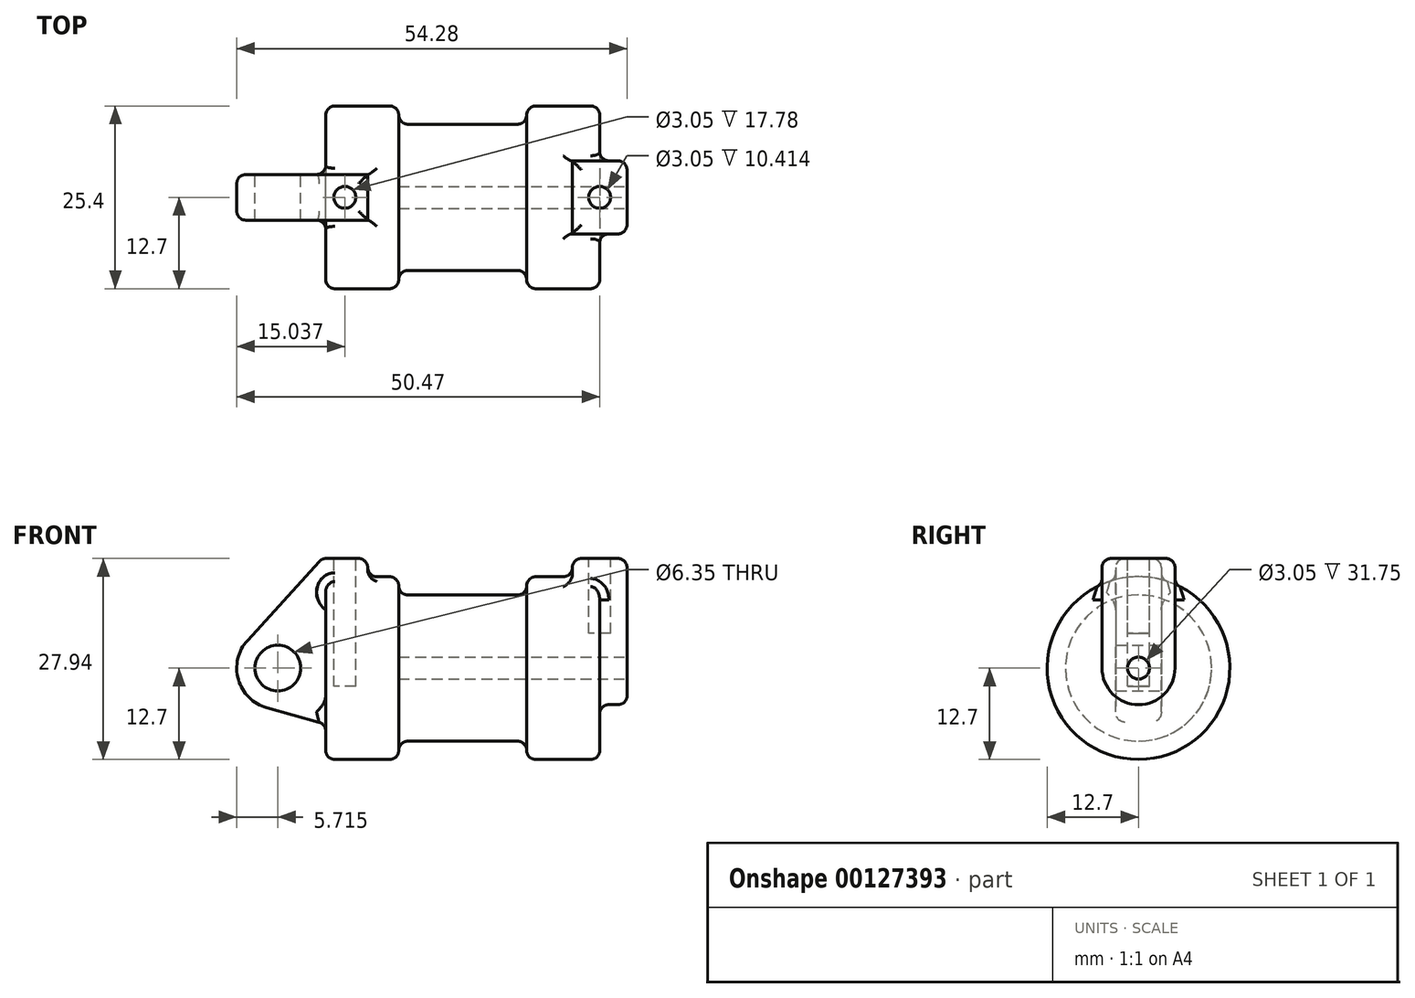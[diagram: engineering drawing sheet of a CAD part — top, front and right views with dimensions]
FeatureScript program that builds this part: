
annotation { "Feature Type Name" : "Feature", "Feature Type Description" : "" }
export const myFeature = defineFeature(function(context is Context, id is Id, definition is map)
    precondition{}
    {
        {
            var Q0;
            Q0=qCreatedBy(makeId("Front.planeOp"),FACE);
            var sketch = newSketch(context, id + "F0", { "sketchPlane" : qUnion([Q0])});
            skLineSegment(sketch, "E0", {"start": v(0, 0) * mm, "end": v(0, 12.7) * mm});
            skLineSegment(sketch, "E1", {"start": v(0, 12.7) * mm, "end": v(10.16, 12.7) * mm});
            skLineSegment(sketch, "E2", {"start": v(10.16, 12.7) * mm, "end": v(10.16, 10.16) * mm});
            skLineSegment(sketch, "E3", {"start": v(10.16, 10.16) * mm, "end": v(27.94, 10.16) * mm});
            skLineSegment(sketch, "E4", {"start": v(27.94, 10.16) * mm, "end": v(27.94, 12.7) * mm});
            skLineSegment(sketch, "E5", {"start": v(27.94, 12.7) * mm, "end": v(38.1, 12.7) * mm});
            skLineSegment(sketch, "E6", {"start": v(38.1, 12.7) * mm, "end": v(38.1, 0) * mm});
            skLineSegment(sketch, "E7", {"start": v(38.1, 0) * mm, "end": v(0, 0) * mm});
            skLineSegment(sketch, "E8", {"start": v(5.84, 15.24) * mm, "end": v(-0.5, 15.24) * mm});
            skLineSegment(sketch, "E9", {"start": v(-0.5, 15.24) * mm, "end": v(-10.88, 3.85) * mm});
            skLineSegment(sketch, "E10", {"start": v(0, 0) * mm, "end": v(-6.65, 0) * mm});
            skCircle(sketch, "E11", {"center": v(-6.65, 0) * mm, "radius": 5.72 * mm});
            skCircle(sketch, "E12", {"center": v(-6.65, 0) * mm, "radius": 3.18 * mm});
            skLineSegment(sketch, "E13", {"start": v(5.84, 15.24) * mm, "end": v(5.84, -9.4) * mm});
            skLineSegment(sketch, "E14", {"start": v(5.84, -9.4) * mm, "end": v(-8.18, -5.5) * mm});
            skSolve(sketch);
        }
        {
            var Q0;
            {var subQ0=sQuery(id+"F0.wireOp",EDGE,"E0");Q0=makeQuery(id+"F0.imprint","IMPRINT",FACE,{"disambiguationData":[TD([[makeQuery(id+"F0.imprint","IMPRINT",EDGE,{"derivedFrom":subQ0}),-1.0]])]});}
            var Q1;
            {var subQ0=sQuery(id+"F0.wireOp",EDGE,"E2");Q1=makeQuery(id+"F0.imprint","IMPRINT",FACE,{"disambiguationData":[TD([[makeQuery(id+"F0.imprint","IMPRINT",EDGE,{"derivedFrom":subQ0}),-1.0]])]});}
            var Q2;
            Q2=sQuery(id+"F0.wireOp",EDGE,"E7");
            revolve(context, id + "F1", {"entities" : qUnion([Q0, Q1]), "axis" : qUnion([Q2]), "revolveType" : RevolveType.FULL});
        }
        {
            var Q0;
            {var subQ3=sQuery(id+"F0.wireOp",EDGE,"E0");Q0=makeQuery(id+"F0.imprint","IMPRINT",FACE,{"disambiguationData":[TD([[makeQuery(id+"F0.imprint","IMPRINT",EDGE,{"derivedFrom":subQ3}),1.0]])]});}
            var Q1;
            {var subQ4=sQuery(id+"F0.wireOp",EDGE,"E12");Q1=makeQuery(id+"F0.imprint","IMPRINT",FACE,{"disambiguationData":[TD([[makeQuery(id+"F0.imprint","IMPRINT",EDGE,{"derivedFrom":subQ4}),-1.0]])]});}
            var Q2;
            {var subQ0=sQuery(id+"F0.wireOp",EDGE,"E14");Q2=makeQuery(id+"F0.imprint","IMPRINT",FACE,{"disambiguationData":[TD([[makeQuery(id+"F0.imprint","IMPRINT",EDGE,{"derivedFrom":subQ0}),-1.0]])]});}
            var Q3;
            {var subQ0=sQuery(id+"F0.wireOp",EDGE,"E0");Q3=makeQuery(id+"F0.imprint","IMPRINT",FACE,{"disambiguationData":[TD([[makeQuery(id+"F0.imprint","IMPRINT",EDGE,{"derivedFrom":subQ0}),-1.0]])]});}
            extrude(context, id + "F2", {"entities" : qUnion([Q0, Q1, Q2, Q3]), "operationType" : NewBodyOperationType.ADD, "endBound" : BoundingType.SYMMETRIC, "depth" : 6.35 * mm});
        }
        {
            var Q0;
            Q0=makeQuery(id+"F1.opRevolve","SWEPT_FACE",FACE,{"disambiguationData":[OSD([sQuery(id+"F0.wireOp",EDGE,"E6")])]});
            var sketch = newSketch(context, id + "F3", { "sketchPlane" : qUnion([Q0])});
            skCircle(sketch, "E15", {"center": v(0, 0) * mm, "radius": 1.52 * mm});
            skCircle(sketch, "E16", {"center": v(0, 0) * mm, "radius": 5.08 * mm});
            skLineSegment(sketch, "E17", {"start": v(-5.08, 0) * mm, "end": v(-5.08, 15.24) * mm});
            skLineSegment(sketch, "E18", {"start": v(-5.08, 15.24) * mm, "end": v(5.08, 15.24) * mm});
            skLineSegment(sketch, "E19", {"start": v(5.08, 15.24) * mm, "end": v(5.08, 0) * mm});
            skSolve(sketch);
        }
        {
            var Q0;
            Q0=makeQuery(id+"F3.imprint","IMPRINT",FACE,{"disambiguationData":[TD([[makeQuery(id+"F3.imprint","IMPRINT",EDGE,{"derivedFrom":sQuery(id+"F3.wireOp",EDGE,"E15")}),1.0]])]});
            var Q1;
            Q1=sQuery(id+"F3.wireOp",EDGE,"E15");
            var Q2;
            Q2=makeQuery(id+"F1.opRevolve","SWEPT_FACE",FACE,{"disambiguationData":[OSD([sQuery(id+"F0.wireOp",EDGE,"E2")])]});
            extrude(context, id + "F4", {"entities" : qUnion([Q0]), "operationType" : NewBodyOperationType.REMOVE, "surfaceEntities" : qUnion([Q1]), "endBound" : BoundingType.UP_TO_SURFACE, "oppositeDirection" : true, "endBoundEntityFace" : qUnion([Q2]), "depth" : 25.4 * mm});
        }
        {
            var Q0;
            {var subQ0=sQuery(id+"F3.wireOp",EDGE,"E18");Q0=makeQuery(id+"F3.imprint","IMPRINT",FACE,{"disambiguationData":[TD([[makeQuery(id+"F3.imprint","IMPRINT",EDGE,{"derivedFrom":subQ0}),-1.0]])]});}
            var Q1;
            {var subQ0=sQuery(id+"F3.wireOp",EDGE,"E17");var subQ1=sQuery(id+"F3.wireOp",EDGE,"E16");var subQ2=makeQuery(id+"F3.imprint","INTERSECT",VERTEX,{"derivedFrom":[subQ1,subQ0]});Q1=makeQuery(id+"F3.imprint","IMPRINT",FACE,{"disambiguationData":[TD([[makeQuery(id+"F3.imprint","IMPRINT",EDGE,{"disambiguationData":[TD([[subQ2,1.0]])],"derivedFrom":subQ1}),-1.0]])]});}
            var Q2;
            Q2=makeQuery(id+"F3.imprint","IMPRINT",FACE,{"disambiguationData":[TD([[makeQuery(id+"F3.imprint","IMPRINT",EDGE,{"derivedFrom":sQuery(id+"F3.wireOp",EDGE,"E15")}),-1.0]])]});
            extrude(context, id + "F5", {"entities" : qUnion([Q0, Q1, Q2]), "operationType" : NewBodyOperationType.ADD, "endBound" : BoundingType.SYMMETRIC, "depth" : 7.62 * mm});
        }
        {
            var Q0;
            Q0=makeQuery(id+"F2.opExtrude","SWEPT_FACE",FACE,{"disambiguationData":[OSD([sQuery(id+"F0.wireOp",EDGE,"E8")])]});
            var sketch = newSketch(context, id + "F6", { "sketchPlane" : qUnion([Q0])});
            skCircle(sketch, "E20", {"center": v(2.67, 0) * mm, "radius": 1.52 * mm});
            skPoint(sketch, "E21", {"position": v(2.67, 3.18) * mm});
            skPoint(sketch, "E22", {"position": v(-0.5, 0) * mm});
            skSolve(sketch);
        }
        {
            var Q0;
            Q0=makeQuery(id+"F6.imprint","IMPRINT",FACE,{"disambiguationData":[TD([[makeQuery(id+"F6.imprint","IMPRINT",EDGE,{"derivedFrom":sQuery(id+"F6.wireOp",EDGE,"E20")}),1.0]])]});
            var Q1;
            Q1=sQuery(id+"F6.wireOp",EDGE,"E20");
            extrude(context, id + "F7", {"entities" : qUnion([Q0]), "operationType" : NewBodyOperationType.REMOVE, "surfaceEntities" : qUnion([Q1]), "oppositeDirection" : true, "depth" : 17.78 * mm});
        }
        {
            var Q0;
            {var subQ0=sQuery(id+"F3.wireOp",EDGE,"E18");Q0=makeQuery(id+"FYsuHnN612AzXy7_2.boolean.opBoolean","MERGE",FACE,{"derivedFrom":[makeQuery(id+"F5.opExtrude","SWEPT_FACE",FACE,{"disambiguationData":[OSD([subQ0])]}),makeQuery(id+"FYsuHnN612AzXy7_2.opExtrude","SWEPT_FACE",FACE,{"disambiguationData":[OSD([subQ0])]})]});}
            var sketch = newSketch(context, id + "F8", { "sketchPlane" : qUnion([Q0])});
            skCircle(sketch, "E23", {"center": v(38.1, 0) * mm, "radius": 1.52 * mm});
            skPoint(sketch, "E24", {"position": v(38.1, 5.08) * mm});
            skPoint(sketch, "E25", {"position": v(34.3, 0) * mm});
            skSolve(sketch);
        }
        {
            var Q0;
            Q0=makeQuery(id+"F8.imprint","IMPRINT",FACE,{"disambiguationData":[TD([[makeQuery(id+"F8.imprint","IMPRINT",EDGE,{"derivedFrom":sQuery(id+"F8.wireOp",EDGE,"E23")}),1.0]])]});
            extrude(context, id + "F9", {"entities" : qUnion([Q0]), "operationType" : NewBodyOperationType.REMOVE, "oppositeDirection" : true, "depth" : 10.4 * mm});
        }
        {
            var Q0;
            Q0=makeQuery(id+"F1.opRevolve","SWEPT_FACE",FACE,{"disambiguationData":[OSD([sQuery(id+"F0.wireOp",EDGE,"E6")])]});
            var Q1;
            Q1=makeQuery(id+"F1.opRevolve","SWEPT_FACE",FACE,{"disambiguationData":[OSD([sQuery(id+"F0.wireOp",EDGE,"E5")])]});
            var Q2;
            Q2=makeQuery(id+"F5.opExtrude","CAP_EDGE",EDGE,{"disambiguationData":[OSD([sQuery(id+"F3.wireOp",EDGE,"E16")])],"isStart":false});
            var Q3;
            Q3=makeQuery(id+"F5.opExtrude","SWEPT_EDGE",EDGE,{"disambiguationData":[OSD([sQuery(id+"F3.wireOp",EDGE,"E18"),sQuery(id+"F3.wireOp",EDGE,"E19")])]});
            var Q4;
            Q4=makeQuery(id+"F5.opExtrude","CAP_EDGE",EDGE,{"disambiguationData":[OSD([sQuery(id+"F3.wireOp",EDGE,"E18")])],"isStart":false});
            var Q5;
            Q5=makeQuery(id+"F5.opExtrude","SWEPT_EDGE",EDGE,{"disambiguationData":[OSD([sQuery(id+"F3.wireOp",EDGE,"E17"),sQuery(id+"F3.wireOp",EDGE,"E18")])]});
            var Q6;
            Q6=makeQuery(id+"F5.opExtrude","CAP_EDGE",EDGE,{"disambiguationData":[OSD([sQuery(id+"F3.wireOp",EDGE,"E18")])],"isStart":true});
            var Q7;
            Q7=makeQuery(id+"F1.opRevolve","SWEPT_EDGE",EDGE,{"disambiguationData":[OSD([sQuery(id+"F0.wireOp",EDGE,"E3"),sQuery(id+"F0.wireOp",EDGE,"E4")])]});
            fillet(context, id + "F10", {"entities" : qUnion([Q0, Q1, Q2, Q3, Q4, Q5, Q6, Q7]), "radius" : 1.27 * mm, "tangentPropagation" : true, "allowEdgeOverflow" : false});
        }
        {
            var Q0;
            Q0=makeQuery(id+"F1.opRevolve","SWEPT_FACE",FACE,{"disambiguationData":[OSD([sQuery(id+"F0.wireOp",EDGE,"E2")])]});
            var Q1;
            Q1=makeQuery(id+"F1.opRevolve","SWEPT_FACE",FACE,{"disambiguationData":[OSD([sQuery(id+"F0.wireOp",EDGE,"E1")])]});
            var Q2;
            Q2=makeQuery(id+"F2.boolean.opBoolean","INTERSECT",EDGE,{"derivedFrom":[makeQuery(id+"F1.opRevolve","SWEPT_FACE",FACE,{"disambiguationData":[OSD([sQuery(id+"F0.wireOp",EDGE,"E0")])]}),makeQuery(id+"F2.opExtrude","SWEPT_FACE",FACE,{"disambiguationData":[OSD([sQuery(id+"F0.wireOp",EDGE,"E14")])]})]});
            var Q3;
            Q3=makeQuery(id+"F2.opExtrude","SWEPT_FACE",FACE,{"disambiguationData":[OSD([sQuery(id+"F0.wireOp",EDGE,"E14")])]});
            var Q4;
            Q4=makeQuery(id+"F2.opExtrude","CAP_EDGE",EDGE,{"disambiguationData":[OSD([sQuery(id+"F0.wireOp",EDGE,"E8")])],"isStart":true});
            var Q5;
            Q5=makeQuery(id+"F2.opExtrude","SWEPT_EDGE",EDGE,{"disambiguationData":[OSD([sQuery(id+"F0.wireOp",EDGE,"E8"),sQuery(id+"F0.wireOp",EDGE,"E9")])]});
            var Q6;
            Q6=makeQuery(id+"F2.opExtrude","CAP_EDGE",EDGE,{"disambiguationData":[OSD([sQuery(id+"F0.wireOp",EDGE,"E8")])],"isStart":false});
            var Q7;
            Q7=makeQuery(id+"F2.opExtrude","SWEPT_EDGE",EDGE,{"disambiguationData":[OSD([sQuery(id+"F0.wireOp",EDGE,"E8"),sQuery(id+"F0.wireOp",EDGE,"E13")])]});
            fillet(context, id + "F11", {"entities" : qUnion([Q0, Q1, Q2, Q3, Q4, Q5, Q6, Q7]), "radius" : 1.27 * mm, "tangentPropagation" : true, "allowEdgeOverflow" : false});
        }
    });
